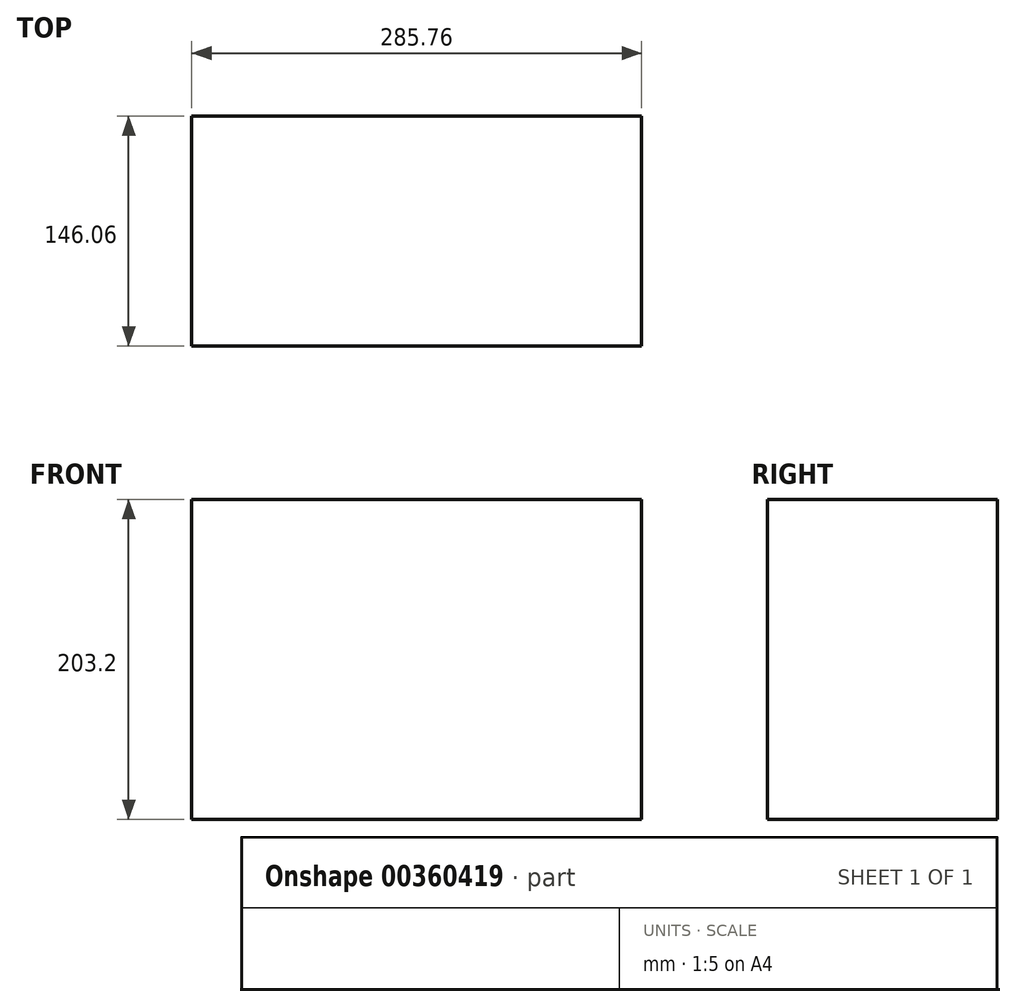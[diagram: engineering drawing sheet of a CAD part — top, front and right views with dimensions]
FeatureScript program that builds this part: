
annotation { "Feature Type Name" : "Feature", "Feature Type Description" : "" }
export const myFeature = defineFeature(function(context is Context, id is Id, definition is map)
    precondition{}
    {
        {
            var Q0;
            Q0=qCreatedBy(makeId("Top.planeOp"),FACE);
            var sketch = newSketch(context, id + "F0", { "sketchPlane" : qUnion([Q0])});
            skLineSegment(sketch, "E0.bottom", {"start": v(142.88, 73.03) * mm, "end": v(-142.88, 73.03) * mm});
            skLineSegment(sketch, "E0.top", {"start": v(142.88, -73.03) * mm, "end": v(-142.88, -73.03) * mm});
            skLineSegment(sketch, "E0.left", {"start": v(142.88, 73.03) * mm, "end": v(142.88, -73.03) * mm});
            skLineSegment(sketch, "E0.right", {"start": v(-142.88, 73.03) * mm, "end": v(-142.88, -73.03) * mm});
            skPoint(sketch, "E0.middle", {"position": v(0, 0) * mm});
            skSolve(sketch);
        }
        {
            var Q0;
            Q0=makeQuery(id+"F0.imprint","IMPRINT",FACE,{"disambiguationData":[TD([[makeQuery(id+"F0.imprint","IMPRINT",EDGE,{"derivedFrom":sQuery(id+"F0.wireOp",EDGE,"E0.bottom")}),1.0]])]});
            extrude(context, id + "F1", {"entities" : qUnion([Q0]), "endBound" : BoundingType.SYMMETRIC, "depth" : 203.2 * mm});
        }
    });
